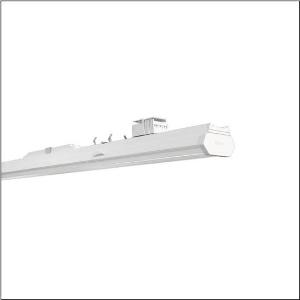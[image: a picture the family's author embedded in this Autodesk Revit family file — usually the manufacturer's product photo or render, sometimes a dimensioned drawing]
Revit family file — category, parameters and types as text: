
# Revit family: licross_r__11_protected_mo_51tp11dn495g_6ace
name_source: partatom
category: Lighting Fixtures
units: mm (PartAtom-declared; Revit-internal decimal feet)

## family parameters
Cut with Voids When Loaded = No
Host = Face
Light Source = No
Part Type = Normal
Room Calculation Point = No
Round Connector Dimension = Use Diameter
Shared = No

## types (1)
- --- (1 x LED, 9930 lm, 57.1 W, 4000K)
    Apparent Load = 57 VA
    CIE Flux Codes = 83 94 98 100 100
    Color Rendering = 80
    Color Temperature = 4000K
    Default Elevation = 1800 mm
    Description = Licross® 11 Protected MO, luminaire insert, of sheet steel, galvanised, coil coated, white, length: 1.500mm, width: 90mm, height: 101mm, LED rated luminous flux: 9.980lm, light colour: 840, control gear: DALI 2, with plug, 5-pole, with phase selection, mains connection: 220..240V, AC, 50/60Hz, rated input power: 57W, halogen-free wiring, primary light control with lens, of plastic, primary optical cover: cover, of PMMA, light emission: direct distribution, primary light characteristic: symmetric, protection rating (complete): IP64, insulation class (complete): insulation class I (protective earthing), certification: CE, ENEC, VDE, UKCA, protection symbol: D if used in an environment with conductive dust loads with corresponding accessories, impact resistance: IK06, permissible ambient temperature for indoor applications: -25..+35°C, corresponds to IFS (International Featured Standards) requirements for safety and quality in the food industry, reducing of maximum allowable ambient temperature of 5°C with ceiling mounting, LABS conformity tested according to VDMA 24364:2018-05, packaging unit: 1 piece
    Height = 92 mm
    Lamp = 1 x LED
    Lamp Light Flux = 9930 lm
    Lamp Power = 57.1 W
    Lamp count = 1
    Length = 1500 mm
    Luminous efficacy = 174 lm/W
    Manufacturer = Siteco
    ModVariant = No
    Model = 51TP11DN495G
    Mounting Place = Ceiling
    Mounting Type = Pendant
    Number of Poles = 1
    OnlyDefault = Yes
    Power Factor = 1
    Product Name = Licross® 11 Protected MO
    Product group = luminaire insert
    ProductGroupID = 901
    Protection Class = Protection class I
    Protection Degree = IP 64
    RLX_Detail_Level = 1
    RLX_Emergency_Light_Flux = 0 lm
    RLX_Emergency_Type = 0
    RLX_Emergency_Type_DB = No
    RlxData = <blob elided: 24241 chars, md5=46844f43>
    Socket = socket
    Standby Power = 0 W
    System Light Flux = 9930 lm
    System Power = 57 W
    Type Comments = factory setting: luminous flux: 100 % | dim-lin: 254 | 378 mA
    Type Image = l_1256148.jpg
    URL = http://relux.com
    VarID = @adj_031057
    Voltage = 0 V
    Weight = 0.00 kg
    Width = 88 mm

## geometry (parser evidence)
native form markers: Blend x4, Sweep x12
no freeform markers — native parametric forms only
